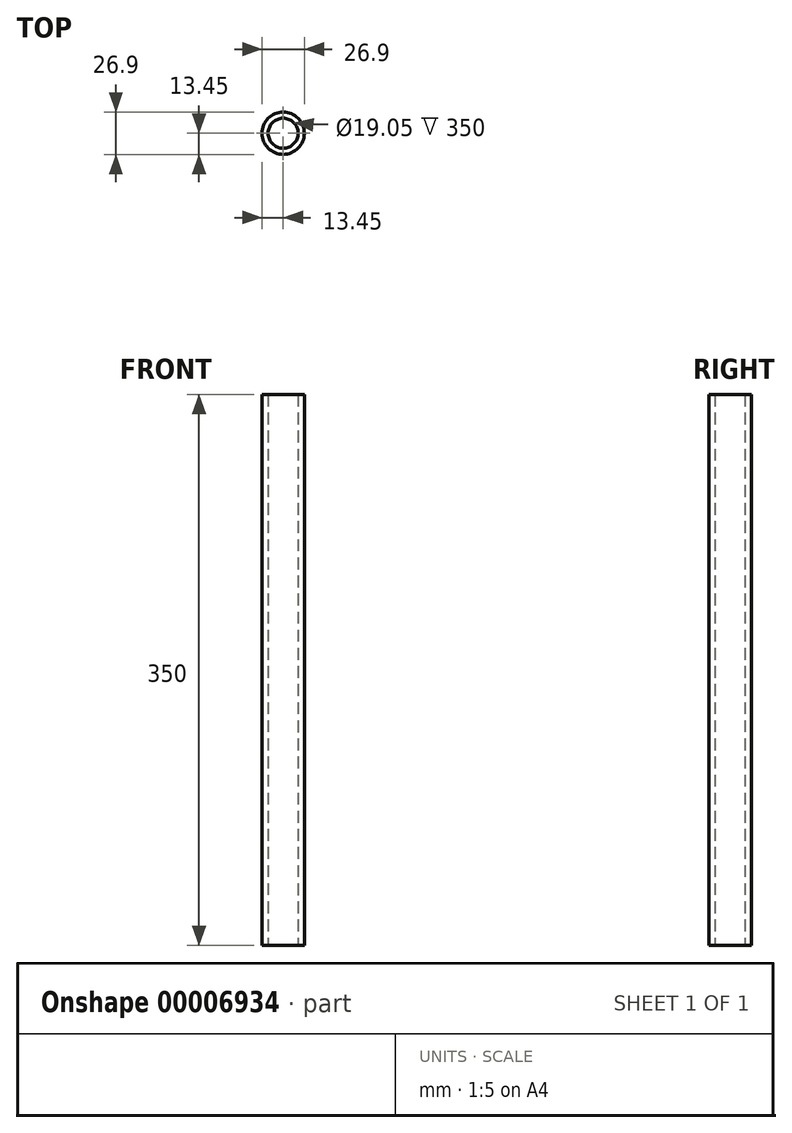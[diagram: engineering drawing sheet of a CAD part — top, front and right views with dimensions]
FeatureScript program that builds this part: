
annotation { "Feature Type Name" : "Feature", "Feature Type Description" : "" }
export const myFeature = defineFeature(function(context is Context, id is Id, definition is map)
    precondition{}
    {
        {
            var Q0;
            Q0=qCreatedBy(makeId("Top.planeOp"),FACE);
            var sketch = newSketch(context, id + "F0", { "sketchPlane" : qUnion([Q0])});
            skCircle(sketch, "E0", {"center": v(0, 0) * mm, "radius": 13.45 * mm});
            skCircle(sketch, "E1", {"center": v(0, 0) * mm, "radius": 9.53 * mm});
            skSolve(sketch);
        }
        {
            var Q0;
            Q0=makeQuery(id+"F0.imprint","IMPRINT",FACE,{"disambiguationData":[TD([[makeQuery(id+"F0.imprint","IMPRINT",EDGE,{"derivedFrom":sQuery(id+"F0.wireOp",EDGE,"E0")}),1.0]])]});
            extrude(context, id + "F1", {"entities" : qUnion([Q0]), "depth" : (350) * mm});
        }
    });
